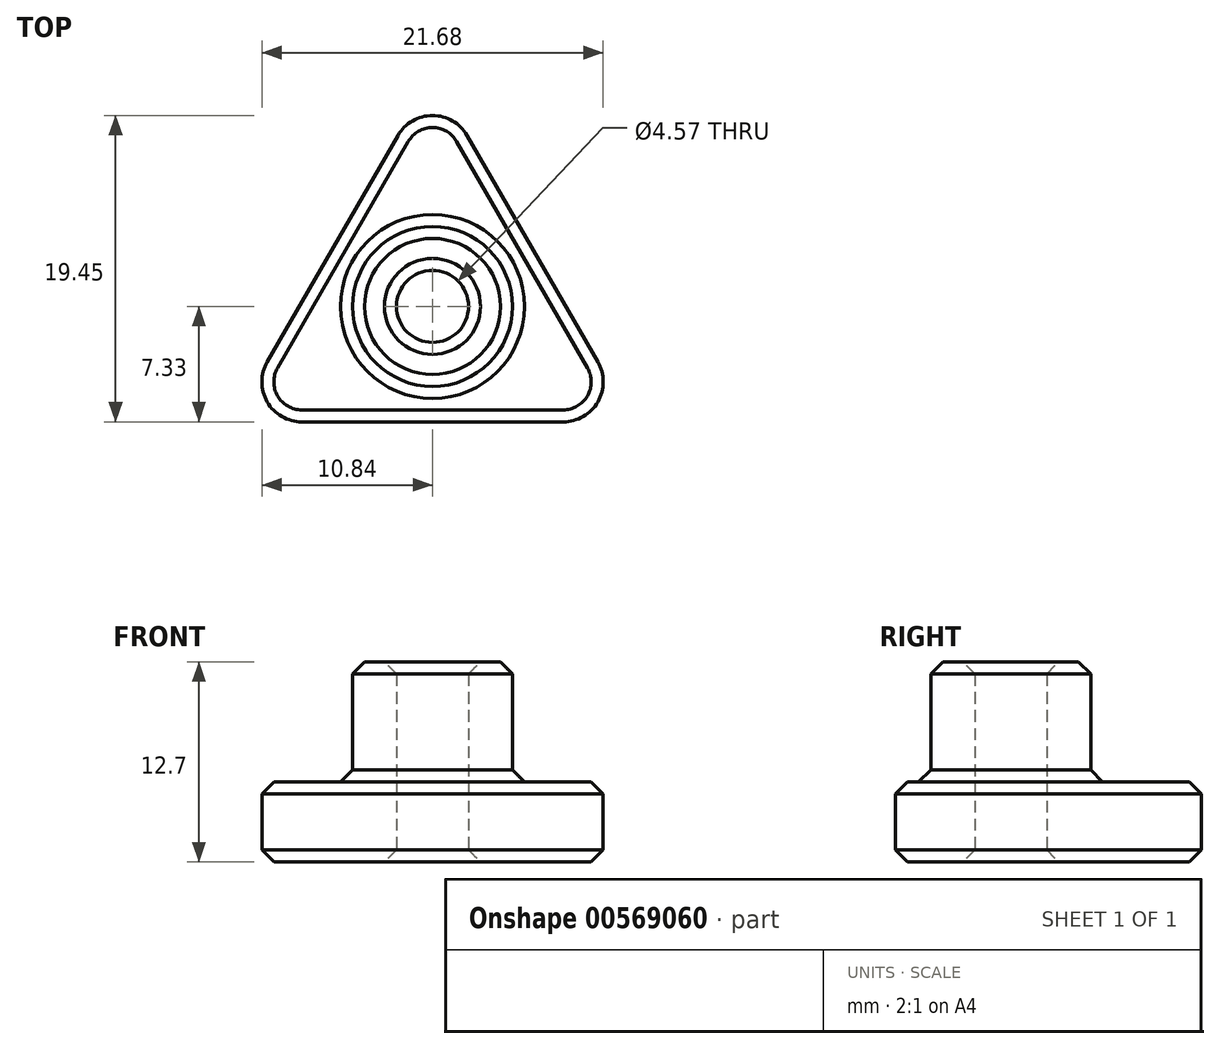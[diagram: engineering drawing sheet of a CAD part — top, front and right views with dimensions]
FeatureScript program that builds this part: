
annotation { "Feature Type Name" : "Feature", "Feature Type Description" : "" }
export const myFeature = defineFeature(function(context is Context, id is Id, definition is map)
    precondition{}
    {
        {
            var Q0;
            Q0=qCreatedBy(makeId("Top.planeOp"),FACE);
            var sketch = newSketch(context, id + "F0", { "sketchPlane" : qUnion([Q0])});
            skLineSegment(sketch, "E0", {"start": v(0, 14.66) * mm, "end": v(12.7, -7.33) * mm});
            skLineSegment(sketch, "E1", {"start": v(12.7, -7.33) * mm, "end": v(-12.7, -7.33) * mm});
            skLineSegment(sketch, "E2", {"start": v(-12.7, -7.33) * mm, "end": v(0, 14.66) * mm});
            skLineSegment(sketch, "E3", {"start": v(-12.7, -7.33) * mm, "end": v(6.35, 3.67) * mm, "construction": true});
            skSolve(sketch);
        }
        {
            var Q0;
            Q0=makeQuery(id+"F0.imprint","IMPRINT",FACE,{"disambiguationData":[TD([[makeQuery(id+"F0.imprint","IMPRINT",EDGE,{"derivedFrom":sQuery(id+"F0.wireOp",EDGE,"E0")}),-1.0]])]});
            extrude(context, id + "F1", {"entities" : qUnion([Q0]), "depth" : 5.08 * mm, "offsetDistance" : 25.4 * mm});
        }
        {
            var Q0;
            Q0=qCreatedBy(makeId("Top.planeOp"),FACE);
            var sketch = newSketch(context, id + "F2", { "sketchPlane" : qUnion([Q0])});
            skCircle(sketch, "E4", {"center": v(0, 0) * mm, "radius": 5.08 * mm});
            skSolve(sketch);
        }
        {
            var Q0;
            Q0 = qSketchRegion(id + "F2", true);
            extrude(context, id + "F3", {"entities" : qUnion([Q0]), "operationType" : NewBodyOperationType.ADD, "depth" : 12.7 * mm, "offsetDistance" : 25.4 * mm});
        }
        {
            var Q0;
            Q0=sQuery(id+"F2.wireOp",VERTEX,"E4.center");
            var Q1;
            Q1=makeQuery(id+"F1.opExtrude","SWEPT_BODY",BODY,{"disambiguationData":[OSD([sQuery(id+"F0.wireOp",EDGE,"E0"),sQuery(id+"F0.wireOp",EDGE,"E1"),sQuery(id+"F0.wireOp",EDGE,"E2")])]});
            hole(context, id + "F4", {"style" : HoleStyle.SIMPLE, "endStyle" : HoleEndStyle.THROUGH, "oppositeDirection" : true, "holeDiameter" : 4.57 * mm, "tappedDepth" : 12.7 * mm, "tapClearance" : 3, "startFromSketch" : true, "locations" : qUnion([Q0]), "scope" : qUnion([Q1])});
        }
        {
            var Q0;
            Q0=makeQuery(id+"F1.opExtrude","SWEPT_EDGE",EDGE,{"disambiguationData":[OSD([sQuery(id+"F0.wireOp",EDGE,"E1"),sQuery(id+"F0.wireOp",EDGE,"E2")])]});
            var Q1;
            Q1=makeQuery(id+"F1.opExtrude","SWEPT_EDGE",EDGE,{"disambiguationData":[OSD([sQuery(id+"F0.wireOp",EDGE,"E0"),sQuery(id+"F0.wireOp",EDGE,"E1")])]});
            var Q2;
            Q2=makeQuery(id+"F1.opExtrude","SWEPT_EDGE",EDGE,{"disambiguationData":[OSD([sQuery(id+"F0.wireOp",EDGE,"E0"),sQuery(id+"F0.wireOp",EDGE,"E2")])]});
            fillet(context, id + "F5", {"entities" : qUnion([Q0, Q1, Q2]), "radius" : 2.54 * mm, "tangentPropagation" : true, "allowEdgeOverflow" : false});
        }
        {
            var Q0;
            Q0=makeQuery(id+"F1.opExtrude","CAP_FACE",FACE,{"disambiguationData":[OSD([sQuery(id+"F0.wireOp",EDGE,"E0"),sQuery(id+"F0.wireOp",EDGE,"E1"),sQuery(id+"F0.wireOp",EDGE,"E2")])],"isStart":true});
            var Q1;
            Q1=makeQuery(id+"F3.opExtrude","CAP_FACE",FACE,{"disambiguationData":[OSD([sQuery(id+"F2.wireOp",EDGE,"E4")])],"isStart":false});
            var Q2;
            Q2=makeQuery(id+"F1.opExtrude","CAP_FACE",FACE,{"disambiguationData":[OSD([sQuery(id+"F0.wireOp",EDGE,"E0"),sQuery(id+"F0.wireOp",EDGE,"E1"),sQuery(id+"F0.wireOp",EDGE,"E2")])],"isStart":false});
            chamfer(context, id + "F6", {"entities" : qUnion([Q0, Q1, Q2]), "width" : 0.76 * mm, "tangentPropagation" : true});
        }
    });
